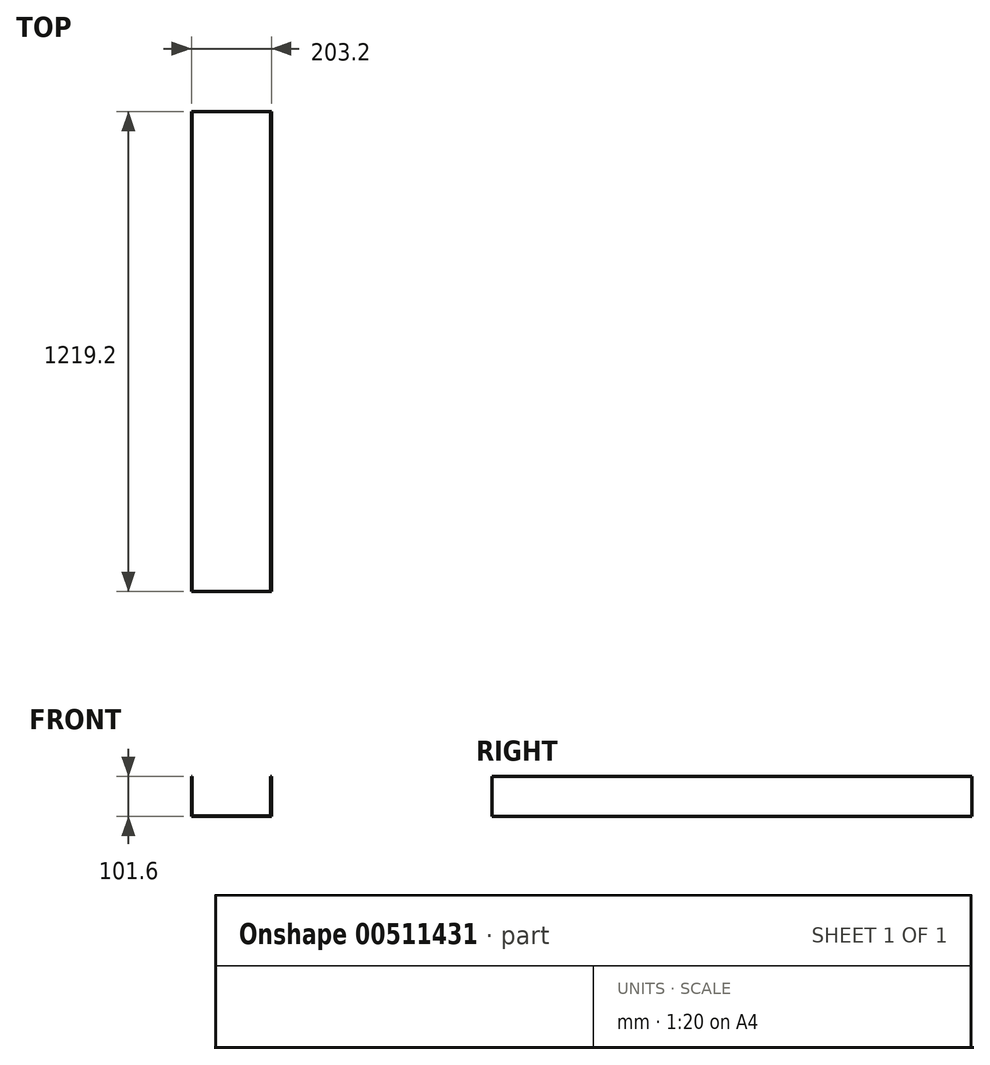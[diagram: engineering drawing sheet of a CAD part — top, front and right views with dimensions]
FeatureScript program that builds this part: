
annotation { "Feature Type Name" : "Feature", "Feature Type Description" : "" }
export const myFeature = defineFeature(function(context is Context, id is Id, definition is map)
    precondition{}
    {
        {
            var Q0;
            Q0=qCreatedBy(makeId("Front.planeOp"),FACE);
            var sketch = newSketch(context, id + "F0", { "sketchPlane" : qUnion([Q0])});
            skLineSegment(sketch, "E0", {"start": v(-94.77, 120.8) * mm, "end": v(-94.77, 20.8) * mm});
            skLineSegment(sketch, "E1", {"start": v(-94.77, 20.8) * mm, "end": v(105.25, 20.8) * mm});
            skLineSegment(sketch, "E2", {"start": v(105.25, 20.8) * mm, "end": v(105.25, 120.8) * mm});
            skLineSegment(sketch, "E3.0", {"start": v(106.84, 19.2) * mm, "end": v(106.84, 127.16) * mm});
            skLineSegment(sketch, "E3.1", {"start": v(-96.36, 19.2) * mm, "end": v(106.84, 19.2) * mm});
            skLineSegment(sketch, "E3.2", {"start": v(-96.36, 127.16) * mm, "end": v(-96.36, 19.2) * mm});
            skLineSegment(sketch, "E4", {"start": v(105.25, 120.8) * mm, "end": v(106.84, 120.8) * mm});
            skLineSegment(sketch, "E5", {"start": v(-94.77, 120.8) * mm, "end": v(-96.36, 120.8) * mm});
            skSolve(sketch);
        }
        {
            var Q0;
            Q0=makeQuery(id+"F0.imprint","IMPRINT",FACE,{"disambiguationData":[TD([[makeQuery(id+"F0.imprint","IMPRINT",EDGE,{"derivedFrom":sQuery(id+"F0.wireOp",EDGE,"E0")}),-1.0]])]});
            extrude(context, id + "F1", {"entities" : qUnion([Q0]), "depth" : 1219.2 * mm});
        }
    });
